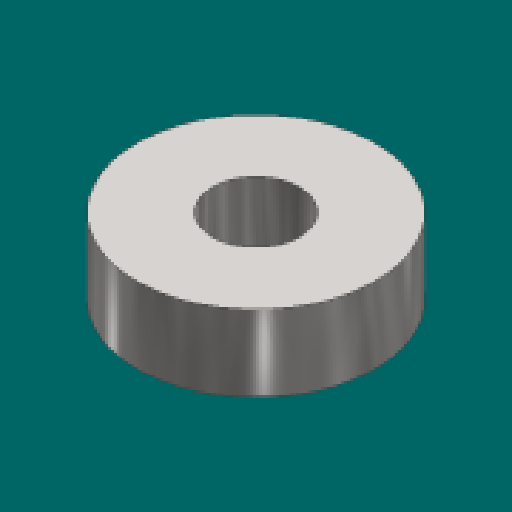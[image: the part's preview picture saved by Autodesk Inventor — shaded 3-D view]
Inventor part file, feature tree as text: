
AUTODESK INVENTOR PART (.ipt)
format: ipt  version: 2023.1 (Build 271208000, 208)  size: 92,672 bytes
history: native  units: in
note: dims shown in document units (in); Inventor stores cm internally (conversion verified against a paired STEP export)
features: extrude x1, sketch x1
ambient origin geometry x8: Origin, YZ Plane, XZ Plane, XY Plane, X Axis, Y Axis, Z Axis, Center Point
bodies: Solid1 (feature_tree)
feature tree (2):
  extrude  "Extrusion1"  Depth=0.2756in
  sketch  "Sketch1"  dims[d0=0.315in d1=0.8661in d2=0.2756in d3=0.0in]
